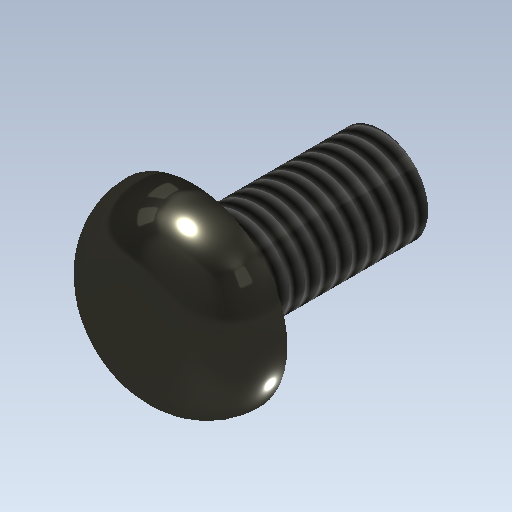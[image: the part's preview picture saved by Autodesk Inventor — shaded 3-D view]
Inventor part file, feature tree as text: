
AUTODESK INVENTOR PART (.ipt)
format: ipt  version: 2020.2 (Build 242310000, 310)  size: 174,080 bytes
history: native  units: mm
features: extrude x2, sketch x2, other x1, fillet x1, thread x1
ambient origin geometry x1: Origin
bodies: Body1 (feature_tree)
feature tree (7):
  other  "ソリッド1"
  extrude  "押し出し1"  Depth=3.0mm
  extrude  "押し出し2"  Depth=6.0mm TaperAngle=0.0deg
  fillet  "フィレット1"  Radius=6.0mm
  thread  "ねじ1"
  sketch  "スケッチ1"
  sketch  "スケッチ2"
